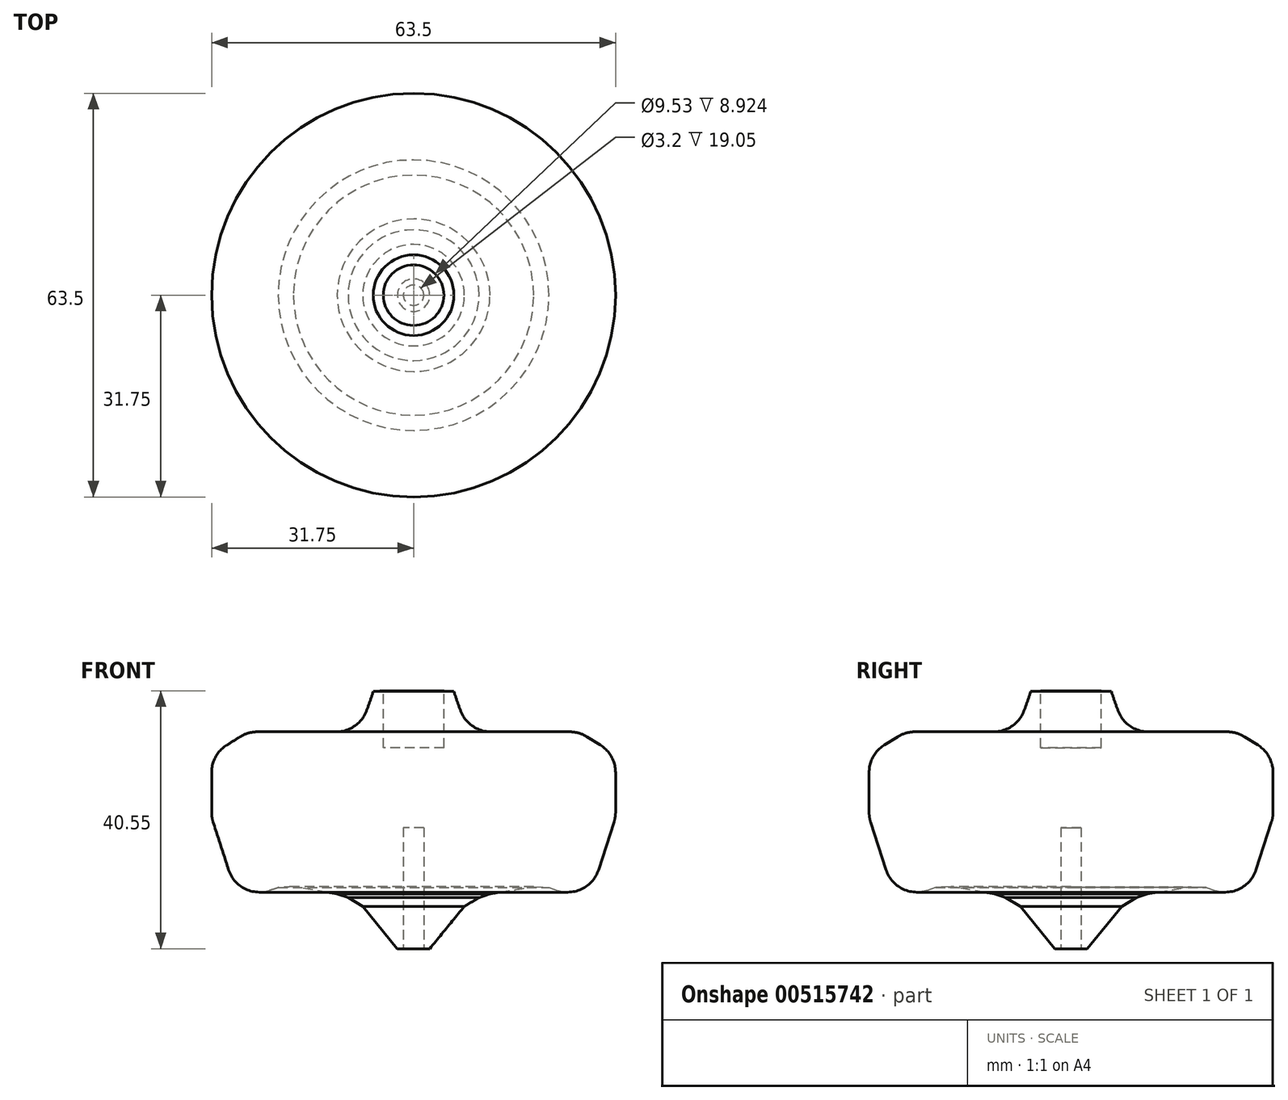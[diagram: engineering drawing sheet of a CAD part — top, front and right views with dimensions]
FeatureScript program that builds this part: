
annotation { "Feature Type Name" : "Feature", "Feature Type Description" : "" }
export const myFeature = defineFeature(function(context is Context, id is Id, definition is map)
    precondition{}
    {
        {
            var Q0;
            Q0=qCreatedBy(makeId("Front.planeOp"),FACE);
            var sketch = newSketch(context, id + "F0", { "sketchPlane" : qUnion([Q0])});
            skLineSegment(sketch, "E0", {"start": v(0, 40.77) * mm, "end": v(0, 0) * mm});
            skArc(sketch, "E1", {"start": v(6.34, 40.47) * mm, "mid": v(7.47, 37.25) * mm, "end": v(8.82, 34.12) * mm});
            skLineSegment(sketch, "E2", {"start": v(0, 0) * mm, "end": v(2.55, 0) * mm});
            skLineSegment(sketch, "E3", {"start": v(2.55, 0) * mm, "end": v(9.2, 8.16) * mm});
            skLineSegment(sketch, "E4", {"start": v(6.34, 40.47) * mm, "end": v(0, 40.77) * mm});
            skLineSegment(sketch, "E5", {"start": v(26.03, 34.12) * mm, "end": v(20.12, 34.12) * mm});
            skLineSegment(sketch, "E6", {"start": v(8.82, 34.12) * mm, "end": v(20.13, 34.12) * mm});
            skPoint(sketch, "E6.startSnap0", {"position": v(23.08, 34.12) * mm});
            skLineSegment(sketch, "E7", {"start": v(20.1, 9.98) * mm, "end": v(27.53, 7.58) * mm});
            skLineSegment(sketch, "E8", {"start": v(31.75, 20.67) * mm, "end": v(31.75, 30.52) * mm});
            skLineSegment(sketch, "E9", {"start": v(26.03, 34.12) * mm, "end": v(31.75, 30.52) * mm});
            skLineSegment(sketch, "E10", {"start": v(27.53, 7.58) * mm, "end": v(31.75, 20.67) * mm});
            skLineSegment(sketch, "E11", {"start": v(9.2, 8.16) * mm, "end": v(20.1, 9.98) * mm});
            skSolve(sketch);
        }
        {
            var Q0;
            Q0=qSketchRegion(id+"F0",true);
            var Q1;
            Q1=sQuery(id+"F0.wireOp",EDGE,"E0");
            revolve(context, id + "F1", {"entities" : qUnion([Q0]), "axis" : qUnion([Q1]), "revolveType" : RevolveType.FULL});
        }
        {
            var Q0;
            Q0=qCreatedBy(makeId("Top.planeOp"),FACE);
            cPlane(context, id + "F2", {"entities" : qUnion([Q0]), "cplaneType" : CPlaneType.OFFSET, "offset" : 41.15 * mm, "width" : 152.4 * mm, "height" : 152.4 * mm});
        }
        {
            var Q0;
            Q0=qCreatedBy(id+"F2.planeOp",FACE);
            var sketch = newSketch(context, id + "F3", { "sketchPlane" : qUnion([Q0])});
            skCircle(sketch, "E12", {"center": v(0, 0) * mm, "radius": 4.76 * mm});
            skSolve(sketch);
        }
        {
            var Q0;
            Q0=qSketchRegion(id+"F3",true);
            extrude(context, id + "F4", {"entities" : qUnion([Q0]), "operationType" : NewBodyOperationType.REMOVE, "oppositeDirection" : true, "depth" : 9.52 * mm, "offsetDistance" : 25.4 * mm});
        }
        {
            var Q0;
            Q0=qCreatedBy(makeId("Top.planeOp"),FACE);
            var sketch = newSketch(context, id + "F5", { "sketchPlane" : qUnion([Q0])});
            skCircle(sketch, "E13", {"center": v(0, 0) * mm, "radius": 1.6 * mm});
            skSolve(sketch);
        }
        {
            var Q0;
            Q0=makeQuery(id+"F5.imprint","IMPRINT",FACE,{"disambiguationData":[TD([[makeQuery(id+"F5.imprint","IMPRINT",EDGE,{"derivedFrom":sQuery(id+"F5.wireOp",EDGE,"E13")}),1.0]])]});
            extrude(context, id + "F6", {"entities" : qUnion([Q0]), "operationType" : NewBodyOperationType.REMOVE, "depth" : 19.05 * mm, "offsetDistance" : 25.4 * mm});
        }
        {
            var Q0;
            Q0=makeQuery(id+"F1.opRevolve","SWEPT_FACE",FACE,{"disambiguationData":[OSD([sQuery(id+"F0.wireOp",EDGE,"E8")])]});
            fillet(context, id + "F7", {"entities" : qUnion([Q0]), "radius" : 5.08 * mm, "tangentPropagation" : true, "allowEdgeOverflow" : false});
        }
        {
            var Q0;
            Q0=makeQuery(id+"F1.opRevolve","SWEPT_FACE",FACE,{"disambiguationData":[OSD([sQuery(id+"F0.wireOp",EDGE,"E10")])]});
            fillet(context, id + "F8", {"entities" : qUnion([Q0]), "radius" : 5.08 * mm, "tangentPropagation" : true, "allowEdgeOverflow" : false});
        }
        {
            var Q0;
            Q0=makeQuery(id+"F1.opRevolve","SWEPT_FACE",FACE,{"disambiguationData":[OSD([sQuery(id+"F0.wireOp",EDGE,"E11")])]});
            chamfer(context, id + "F9", {"entities" : qUnion([Q0]), "width" : 5.08 * mm, "tangentPropagation" : true});
        }
        {
            var Q0;
            {var subQ0=sQuery(id+"F0.wireOp",EDGE,"E11");Q0=makeQuery(id+"F9.opChamfer","BLEND_EDGE",EDGE,{"blendedFrom":[makeQuery(id+"F1.opRevolve","SWEPT_EDGE",EDGE,{"disambiguationData":[OSD([sQuery(id+"F0.wireOp",EDGE,"E3"),subQ0])]}),makeQuery(id+"F1.opRevolve","SWEPT_FACE",FACE,{"disambiguationData":[OSD([subQ0])]})],"blendedInto":[makeQuery(id+"F1.opRevolve","SWEPT_FACE",FACE,{"disambiguationData":[OSD([subQ0])]})]});}
            chamfer(context, id + "F10", {"entities" : qUnion([Q0]), "width" : 5.08 * mm, "tangentPropagation" : true});
        }
        {
            var Q0;
            Q0=makeQuery(id+"F1.opRevolve","SWEPT_FACE",FACE,{"disambiguationData":[OSD([sQuery(id+"F0.wireOp",EDGE,"E5"),sQuery(id+"F0.wireOp",EDGE,"E6")])]});
            fillet(context, id + "F11", {"entities" : qUnion([Q0]), "radius" : 5.08 * mm, "tangentPropagation" : true, "allowEdgeOverflow" : false});
        }
    });
